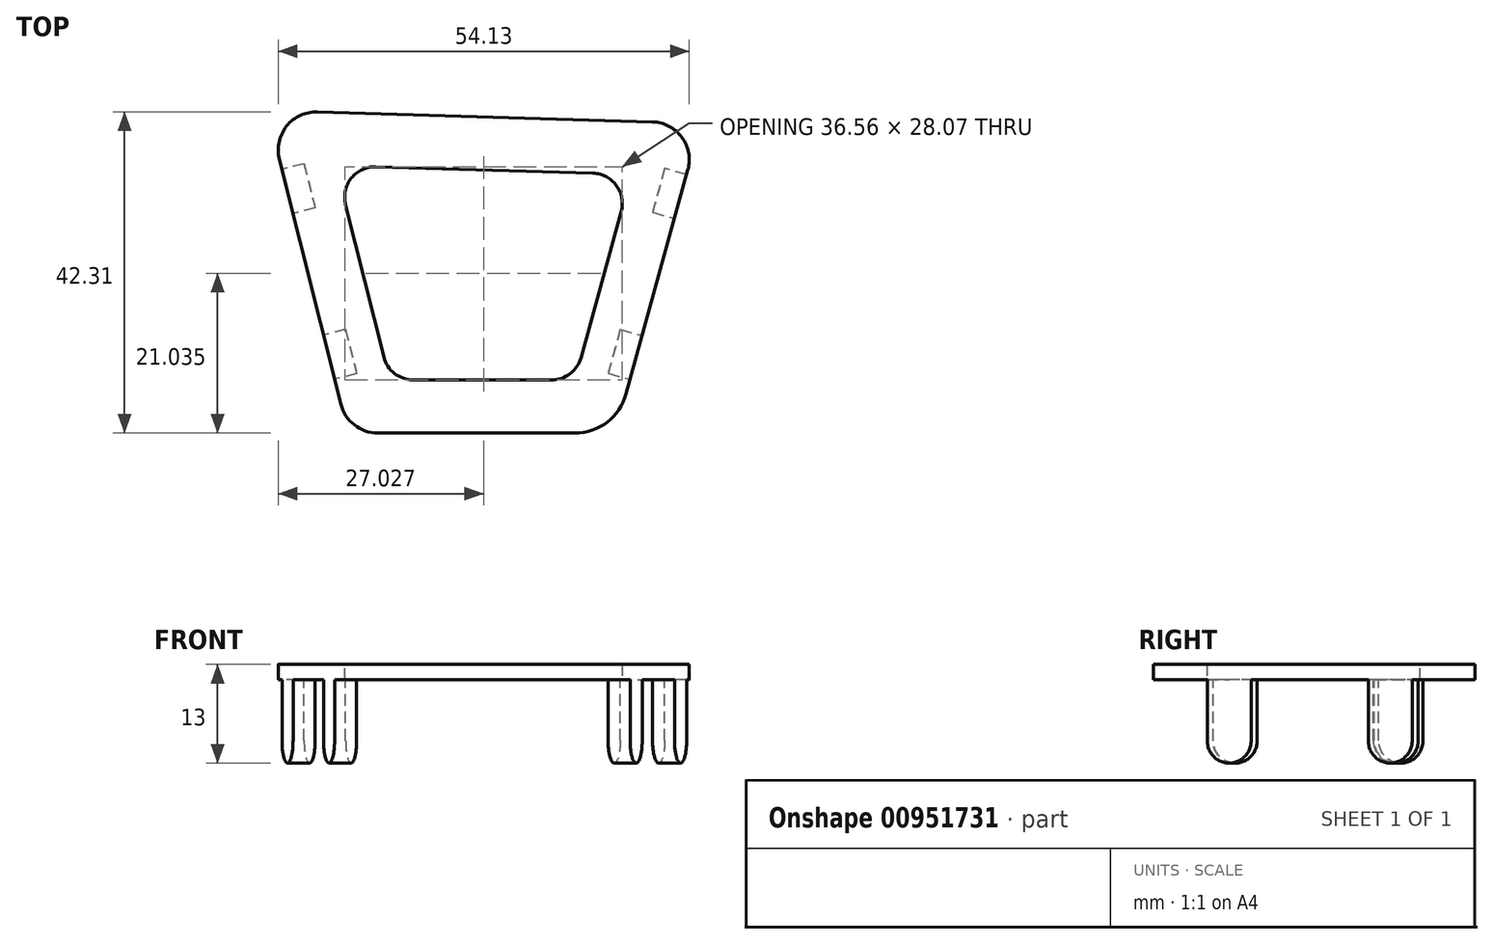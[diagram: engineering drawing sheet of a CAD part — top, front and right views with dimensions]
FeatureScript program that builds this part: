
annotation { "Feature Type Name" : "Feature", "Feature Type Description" : "" }
export const myFeature = defineFeature(function(context is Context, id is Id, definition is map)
    precondition{}
    {
        {
            var Q0;
            Q0=qCreatedBy(makeId("Top.planeOp"),FACE);
            var sketch = newSketch(context, id + "F0", { "sketchPlane" : qUnion([Q0])});
            skLineSegment(sketch, "E0.bottom", {"start": v(28.25, 42) * mm, "end": v(-28.25, 42) * mm, "construction": true});
            skLineSegment(sketch, "E0.top", {"start": v(17.6, 0) * mm, "end": v(-17.6, 0) * mm, "construction": true});
            skPoint(sketch, "E0.middle", {"position": v(0, 0) * mm});
            skLineSegment(sketch, "E1", {"start": v(-28.25, 42) * mm, "end": v(-17.6, 0) * mm, "construction": true});
            skLineSegment(sketch, "E2.MirrorCS", {"start": v(28.25, 42) * mm, "end": v(17.6, 0) * mm, "construction": true});
            skPoint(sketch, "E3", {"position": v(-22.92, 21) * mm});
            skPoint(sketch, "E4", {"position": v(22.93, 21) * mm});
            skSolve(sketch);
        }
        {
            var Q0;
            Q0=qCreatedBy(makeId("Top.planeOp"),FACE);
            var sketch = newSketch(context, id + "F1", { "sketchPlane" : qUnion([Q0])});
            skLineSegment(sketch, "E5.0", {"start": v(-26.64, 36.1) * mm, "end": v(-18.55, 3.78) * mm});
            skLineSegment(sketch, "E5.1", {"start": v(22.49, 40.99) * mm, "end": v(-21.64, 42.3) * mm});
            skLineSegment(sketch, "E5.2", {"start": v(27.16, 34.66) * mm, "end": v(19.02, 5.14) * mm});
            skLineSegment(sketch, "E5.3", {"start": v(12.27, 0) * mm, "end": v(-13.7, 0) * mm});
            skPoint(sketch, "E6.visualSharp", {"position": v(-28.25, 42.5) * mm});
            skArc(sketch, "E6.filletArc", {"start": v(-21.64, 42.3) * mm, "mid": v(-25.69, 40.44) * mm, "end": v(-26.64, 36.1) * mm});
            skPoint(sketch, "E7.visualSharp", {"position": v(-17.6, 0) * mm});
            skArc(sketch, "E7.filletArc", {"start": v(-18.55, 3.78) * mm, "mid": v(-16.77, 1.06) * mm, "end": v(-13.7, 0) * mm});
            skPoint(sketch, "E8.visualSharp", {"position": v(17.6, 0) * mm});
            skArc(sketch, "E8.filletArc", {"start": v(12.27, 0) * mm, "mid": v(16.51, 1.43) * mm, "end": v(19.02, 5.14) * mm});
            skPoint(sketch, "E9.visualSharp", {"position": v(28.85, 40.8) * mm});
            skArc(sketch, "E9.filletArc", {"start": v(27.16, 34.66) * mm, "mid": v(26.36, 38.96) * mm, "end": v(22.49, 40.99) * mm});
            skPoint(sketch, "E10", {"position": v(26.2, 31.16) * mm});
            skPoint(sketch, "E11", {"position": v(23.27, 20.56) * mm});
            skPoint(sketch, "E12", {"position": v(20.34, 9.95) * mm});
            skPoint(sketch, "E13", {"position": v(-25.58, 31.83) * mm});
            skPoint(sketch, "E14", {"position": v(-22.66, 20.19) * mm});
            skPoint(sketch, "E15", {"position": v(-20.1, 10) * mm});
            skSolve(sketch);
        }
        {
            var Q0;
            Q0=qSketchRegion(id+"F1",true);
            extrude(context, id + "F2", {"entities" : qUnion([Q0]), "depth" : 2 * mm});
        }
        {
            var Q0;
            Q0=makeQuery(id+"F2.opExtrude","CAP_FACE",FACE,{"disambiguationData":[OSD([sQuery(id+"F1.wireOp",EDGE,"E5.0"),sQuery(id+"F1.wireOp",EDGE,"E5.1"),sQuery(id+"F1.wireOp",EDGE,"E5.2"),sQuery(id+"F1.wireOp",EDGE,"E5.3"),sQuery(id+"F1.wireOp",EDGE,"E6.filletArc"),sQuery(id+"F1.wireOp",EDGE,"1c2841c0-6afc-4603-80f9-965d2f8b2749.filletArc"),sQuery(id+"F1.wireOp",EDGE,"E7.filletArc"),sQuery(id+"F1.wireOp",EDGE,"E8.filletArc")])],"isStart":false});
            var Q1;
            Q1=makeQuery(id+"F2.opExtrude","CAP_FACE",FACE,{"disambiguationData":[OSD([sQuery(id+"F1.wireOp",EDGE,"E5.0"),sQuery(id+"F1.wireOp",EDGE,"E5.1"),sQuery(id+"F1.wireOp",EDGE,"E5.2"),sQuery(id+"F1.wireOp",EDGE,"E5.3"),sQuery(id+"F1.wireOp",EDGE,"E6.filletArc"),sQuery(id+"F1.wireOp",EDGE,"1c2841c0-6afc-4603-80f9-965d2f8b2749.filletArc"),sQuery(id+"F1.wireOp",EDGE,"E7.filletArc"),sQuery(id+"F1.wireOp",EDGE,"E8.filletArc")])],"isStart":true});
            shell(context, id + "F3", {"entities" : qUnion([Q0, Q1]), "thickness" : 7 * mm});
        }
        {
            var Q0;
            Q0=makeQuery(id+"F3.opShell","OFFSET_EDGE",EDGE,{"disambiguationData":[OSD([sQuery(id+"F1.wireOp",EDGE,"E5.1"),sQuery(id+"F1.wireOp",EDGE,"E5.2"),sQuery(id+"F1.wireOp",EDGE,"1c2841c0-6afc-4603-80f9-965d2f8b2749.filletArc")])]});
            var Q1;
            Q1=makeQuery(id+"F3.opShell","OFFSET_EDGE",EDGE,{"disambiguationData":[OSD([sQuery(id+"F1.wireOp",EDGE,"E5.0"),sQuery(id+"F1.wireOp",EDGE,"E5.1"),sQuery(id+"F1.wireOp",EDGE,"E6.filletArc")])]});
            var Q2;
            Q2=makeQuery(id+"F3.opShell","OFFSET_EDGE",EDGE,{"disambiguationData":[OSD([sQuery(id+"F1.wireOp",EDGE,"E5.0"),sQuery(id+"F1.wireOp",EDGE,"E5.3"),sQuery(id+"F1.wireOp",EDGE,"E7.filletArc")])]});
            var Q3;
            Q3=makeQuery(id+"F3.opShell","OFFSET_EDGE",EDGE,{"disambiguationData":[OSD([sQuery(id+"F1.wireOp",EDGE,"E5.2"),sQuery(id+"F1.wireOp",EDGE,"E5.3"),sQuery(id+"F1.wireOp",EDGE,"E8.filletArc")])]});
            fillet(context, id + "F4", {"entities" : qUnion([Q0, Q1, Q2, Q3]), "radius" : 4 * mm, "tangentPropagation" : true, "allowEdgeOverflow" : false});
        }
        {
            var Q0;
            Q0=makeQuery(id+"F1.imprint","IMPRINT",FACE,{"disambiguationData":[TD([[makeQuery(id+"F1.imprint","IMPRINT",EDGE,{"derivedFrom":sQuery(id+"F1.wireOp",EDGE,"E5.0")}),1.0]])]});
            var sketch = newSketch(context, id + "F5", { "sketchPlane" : qUnion([Q0])});
            skLineSegment(sketch, "E16.0", {"start": v(-26.3, 34.74) * mm, "end": v(-24.85, 28.92) * mm});
            skLineSegment(sketch, "E17.0", {"start": v(26.99, 34.05) * mm, "end": v(25.4, 28.27) * mm});
            skLineSegment(sketch, "E18", {"start": v(-23.4, 35.47) * mm, "end": v(-21.94, 29.65) * mm});
            skLineSegment(sketch, "E19", {"start": v(-23.4, 35.47) * mm, "end": v(-26.3, 34.74) * mm});
            skLineSegment(sketch, "E20", {"start": v(-16.47, 7.82) * mm, "end": v(-19.38, 7.1) * mm});
            skLineSegment(sketch, "E21", {"start": v(26.99, 34.05) * mm, "end": v(24.1, 34.85) * mm});
            skLineSegment(sketch, "E22", {"start": v(24.1, 34.85) * mm, "end": v(22.5, 29.07) * mm});
            skLineSegment(sketch, "E23", {"start": v(16.65, 7.86) * mm, "end": v(19.55, 7.06) * mm});
            skLineSegment(sketch, "E24", {"start": v(22.5, 29.07) * mm, "end": v(25.4, 28.27) * mm});
            skLineSegment(sketch, "E25", {"start": v(18.25, 13.64) * mm, "end": v(21.14, 12.84) * mm});
            skLineSegment(sketch, "E26.trimOffspring", {"start": v(18.25, 13.64) * mm, "end": v(16.65, 7.86) * mm});
            skLineSegment(sketch, "E27.trimOffspring", {"start": v(21.14, 12.84) * mm, "end": v(19.55, 7.06) * mm});
            skLineSegment(sketch, "E28", {"start": v(-21.94, 29.65) * mm, "end": v(-24.85, 28.92) * mm});
            skLineSegment(sketch, "E29", {"start": v(-17.93, 13.64) * mm, "end": v(-20.84, 12.91) * mm});
            skLineSegment(sketch, "E30.trimOffspring", {"start": v(-17.93, 13.64) * mm, "end": v(-16.47, 7.82) * mm});
            skLineSegment(sketch, "E31.trimOffspring", {"start": v(-20.84, 12.91) * mm, "end": v(-19.38, 7.1) * mm});
            skPoint(sketch, "E32.orphan", {"position": v(-26.64, 36.1) * mm});
            skPoint(sketch, "E33.orphan", {"position": v(-18.55, 3.78) * mm});
            skSolve(sketch);
        }
        {
            var Q0;
            Q0=qSketchRegion(id+"F5",true);
            extrude(context, id + "F6", {"entities" : qUnion([Q0]), "operationType" : NewBodyOperationType.ADD, "oppositeDirection" : true, "depth" : 11 * mm});
        }
        {
            var Q0;
            Q0=makeQuery(id+"F6.opExtrude","CAP_EDGE",EDGE,{"disambiguationData":[OSD([sQuery(id+"F5.wireOp",EDGE,"E21")])],"isStart":false});
            var Q1;
            Q1=makeQuery(id+"F6.opExtrude","CAP_EDGE",EDGE,{"disambiguationData":[OSD([sQuery(id+"F5.wireOp",EDGE,"E24")])],"isStart":false});
            var Q2;
            Q2=makeQuery(id+"F6.opExtrude","CAP_EDGE",EDGE,{"disambiguationData":[OSD([sQuery(id+"F5.wireOp",EDGE,"E25")])],"isStart":false});
            var Q3;
            Q3=makeQuery(id+"F6.opExtrude","CAP_EDGE",EDGE,{"disambiguationData":[OSD([sQuery(id+"F5.wireOp",EDGE,"E23")])],"isStart":false});
            var Q4;
            Q4=makeQuery(id+"F6.opExtrude","CAP_EDGE",EDGE,{"disambiguationData":[OSD([sQuery(id+"F5.wireOp",EDGE,"E20")])],"isStart":false});
            var Q5;
            Q5=makeQuery(id+"F6.opExtrude","CAP_EDGE",EDGE,{"disambiguationData":[OSD([sQuery(id+"F5.wireOp",EDGE,"E29")])],"isStart":false});
            var Q6;
            Q6=makeQuery(id+"F6.opExtrude","CAP_EDGE",EDGE,{"disambiguationData":[OSD([sQuery(id+"F5.wireOp",EDGE,"E28")])],"isStart":false});
            var Q7;
            Q7=makeQuery(id+"F6.opExtrude","CAP_EDGE",EDGE,{"disambiguationData":[OSD([sQuery(id+"F5.wireOp",EDGE,"E19")])],"isStart":false});
            fillet(context, id + "F7", {"entities" : qUnion([Q0, Q1, Q2, Q3, Q4, Q5, Q6, Q7]), "radius" : 3 * mm, "tangentPropagation" : true, "allowEdgeOverflow" : false});
        }
    });
